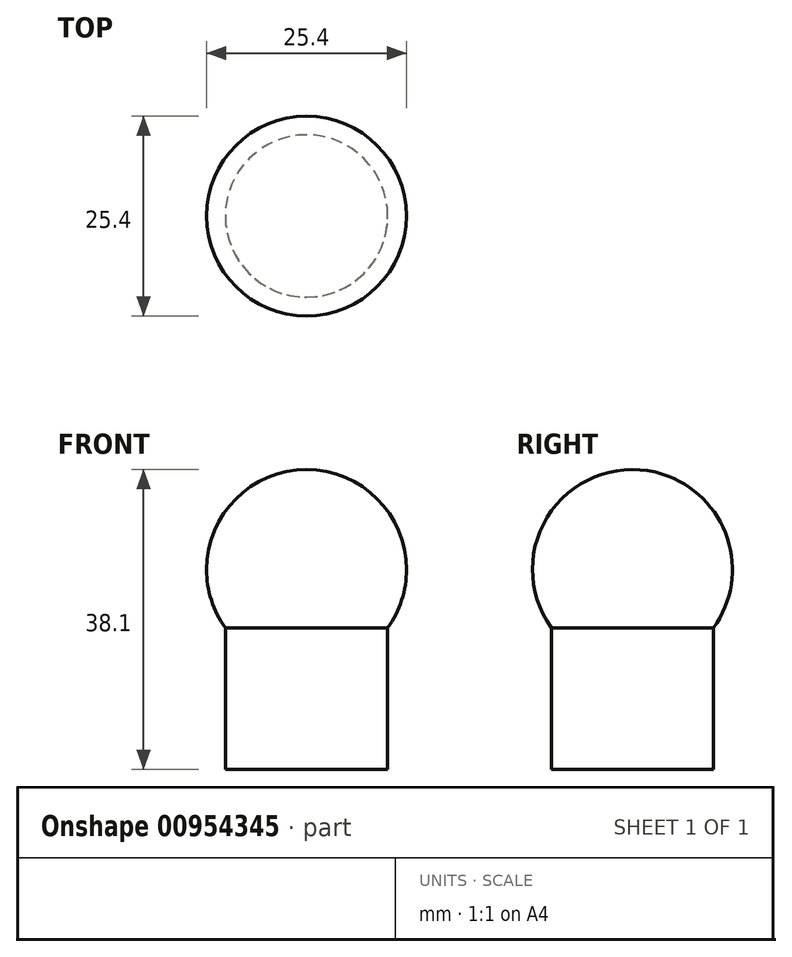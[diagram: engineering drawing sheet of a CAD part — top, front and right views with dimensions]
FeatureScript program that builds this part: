
annotation { "Feature Type Name" : "Feature", "Feature Type Description" : "" }
export const myFeature = defineFeature(function(context is Context, id is Id, definition is map)
    precondition{}
    {
        {
            var Q0;
            Q0=qCreatedBy(makeId("Top.planeOp"),FACE);
            var sketch = newSketch(context, id + "F0", { "sketchPlane" : qUnion([Q0])});
            skCircle(sketch, "E0", {"center": v(0, 0) * mm, "radius": 12.7 * mm});
            skLineSegment(sketch, "E1", {"start": v(-12.7, 0) * mm, "end": v(0, 0) * mm});
            skLineSegment(sketch, "E2", {"start": v(12.7, 0) * mm, "end": v(0, 0) * mm});
            skSolve(sketch);
        }
        {
            var Q0;
            Q0=qCreatedBy(makeId("Front.planeOp"),FACE);
            var sketch = newSketch(context, id + "F1", { "sketchPlane" : qUnion([Q0])});
            skLineSegment(sketch, "E3.bottom", {"start": v(-8.74, 0) * mm, "end": v(10.31, 0) * mm});
            skLineSegment(sketch, "E3.top", {"start": v(-8.74, -25.4) * mm, "end": v(10.31, -25.4) * mm});
            skLineSegment(sketch, "E3.left", {"start": v(-8.74, 0) * mm, "end": v(-8.74, -25.4) * mm});
            skLineSegment(sketch, "E3.right", {"start": v(10.31, 0) * mm, "end": v(10.31, -25.4) * mm});
            skSolve(sketch);
        }
        {
            var Q0;
            Q0=makeQuery(id+"F1.imprint","IMPRINT",FACE,{"disambiguationData":[TD([[makeQuery(id+"F1.imprint","IMPRINT",EDGE,{"derivedFrom":sQuery(id+"F1.wireOp",EDGE,"E3.bottom")}),-1.0]])]});
            var sketch = newSketch(context, id + "F2", { "sketchPlane" : qUnion([Q0])});
            skLineSegment(sketch, "E4", {"start": v(0, -25.47) * mm, "end": v(0, 0) * mm});
            skSolve(sketch);
        }
        {
            var Q0;
            {var subQ5=makeQuery(id+"F1.imprint","IMPRINT",EDGE,{"derivedFrom":sQuery(id+"F1.wireOp",EDGE,"E3.right")});Q0=makeQuery(id+"F2.imprint","IMPRINT",FACE,{"disambiguationData":[TD([[makeQuery(id+"F2.imprint","IMPRINT",EDGE,{"derivedFrom":subQ5}),-1.0]])]});}
            var Q1;
            Q1=sQuery(id+"F2.wireOp",EDGE,"E4");
            revolve(context, id + "F3", {"surfaceOperationType" : NewSurfaceOperationType.NEW, "entities" : qUnion([Q0]), "axis" : qUnion([Q1]), "revolveType" : RevolveType.FULL});
        }
        {
            var Q0;
            {var subQ0=sQuery(id+"F0.wireOp",EDGE,"E1");Q0=makeQuery(id+"F0.imprint","IMPRINT",FACE,{"disambiguationData":[TD([[makeQuery(id+"F0.imprint","IMPRINT",EDGE,{"derivedFrom":subQ0}),1.0]])]});}
            var Q1;
            Q1=sQuery(id+"F0.wireOp",EDGE,"E0");
            var Q2;
            Q2=sQuery(id+"F1.wireOp",EDGE,"E3.bottom");
            revolve(context, id + "F4", {"operationType" : NewBodyOperationType.ADD, "surfaceOperationType" : NewSurfaceOperationType.NEW, "entities" : qUnion([Q0]), "surfaceEntities" : qUnion([Q1]), "axis" : qUnion([Q2]), "revolveType" : RevolveType.FULL, "oppositeDirection" : true});
        }
    });
